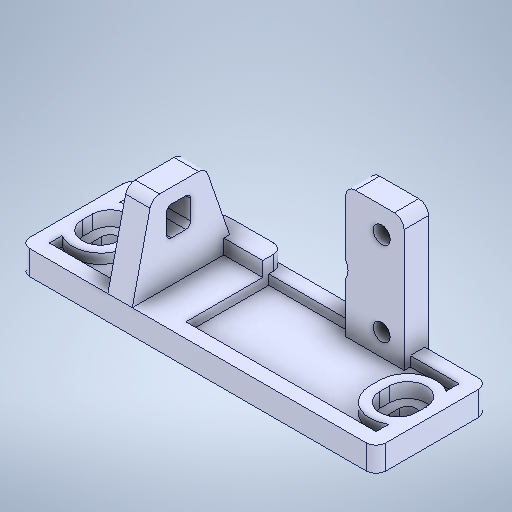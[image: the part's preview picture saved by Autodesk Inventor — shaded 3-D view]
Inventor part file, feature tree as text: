
AUTODESK INVENTOR PART (.ipt)
format: ipt  version: 2025.1 (Build 291241020, 241B)  size: 397,312 bytes
history: native  units: mm
features: fillet x1, other x1
ambient origin geometry x8: Origin, YZ Plane, XZ Plane, XY Plane, X Axis, Y Axis, Z Axis, Center Point
bodies: Solid1 (feature_tree), Solid2 (feature_tree)
feature tree (2):
  fillet  "Fillet5"  [1 undecoded]
  other  "Body-Move_Copy1"
note: 1 required parameter value undecoded (feature->parameter linkage not recoverable at this tier; creation-order binding heuristic only, values carry confidence <= 0.55)
